# Revit family: EKF450E1 BIM position 3
name_source: partatom
category: Mechanical Equipment
revit_build: Autodesk Revit MEP 2013 (Build: 20120221_2030(x64)
units: mm (PartAtom-declared; Revit-internal decimal feet)

## types (1)
- EKF450E1
    AC Frequency Input = 50Hz nominal
    AC Voltage Input = 220-240 V AC (single phase)
    Category = Lo-Carbon Kitchen Box Fan
    Country of Manufacture = UK
    Family = In-Line Range
    Height = 700 mm
220mm
    IP Rating = IP54
    Length (excluding Spigots) = 826 mm
    Length (including Spigots = 700 mm
    Manufacturer - Name = Vent-Axia Ltd
    Manufacturer - Website = www.vent-axia.com
    Maximum In-Duct Temperature = 120 Degrees C
    Motor Rating = 0.99kW Max
    Operating Temperature = (-20C to +40C)
    Operational and Maintenance Manual = http://www.vent-axia.com
    Options = Weatherproofed and Constant Pressure options
    Part Number = EKF450E1
    Product Description = Lo-Carbon Kitchen Box Fan
    Sub Type = Lo-Carbon Kitchen Box Fan
    Warranty period = Unit 2 years                                    Motor 5 years
    Weight = 83.5 kg
    Width (excluding controller) = 700 mm
    Width (including controller) = 784 mm

## geometry (parser evidence)
native form markers: Sweep x1
no freeform markers — native parametric forms only
